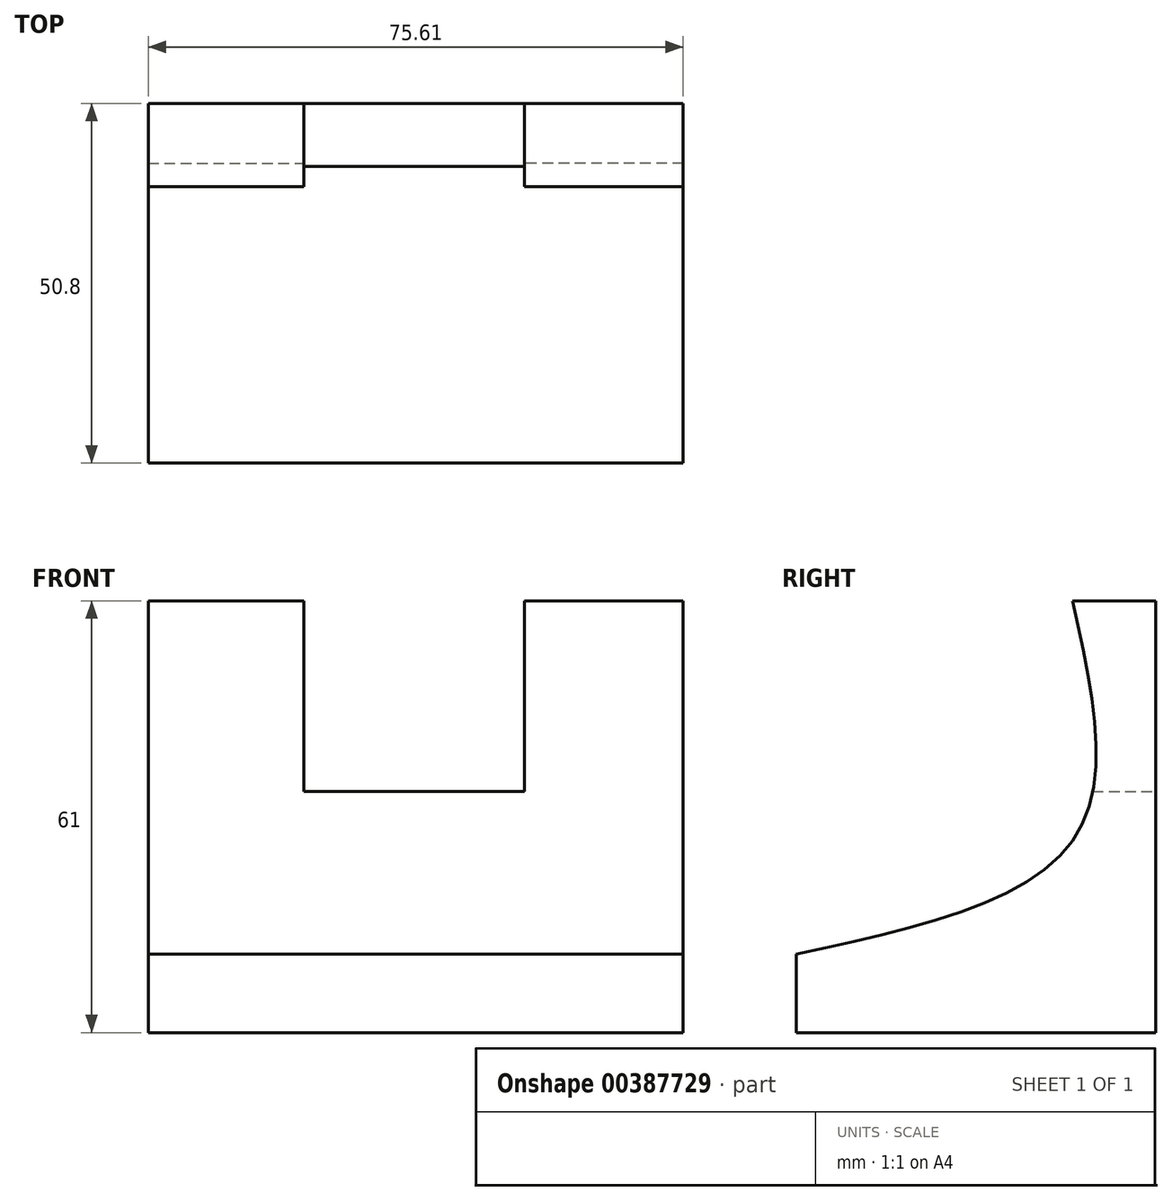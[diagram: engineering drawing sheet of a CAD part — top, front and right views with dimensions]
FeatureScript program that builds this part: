
annotation { "Feature Type Name" : "Feature", "Feature Type Description" : "" }
export const myFeature = defineFeature(function(context is Context, id is Id, definition is map)
    precondition{}
    {
        {
            var Q0;
            Q0=qCreatedBy(makeId("Front.planeOp"),FACE);
            var sketch = newSketch(context, id + "F0", { "sketchPlane" : qUnion([Q0])});
            skLineSegment(sketch, "E0", {"start": v(0, 0) * mm, "end": v(0, 61) * mm});
            skLineSegment(sketch, "E1", {"start": v(0, 61) * mm, "end": v(75.61, 61) * mm});
            skLineSegment(sketch, "E2", {"start": v(75.61, 61) * mm, "end": v(75.61, 0) * mm});
            skLineSegment(sketch, "E3", {"start": v(75.61, 0) * mm, "end": v(0, 0) * mm});
            skSolve(sketch);
        }
        {
            var Q0;
            Q0 = qSketchRegion(id + "F0", true);
            extrude(context, id + "F1", {"entities" : qUnion([Q0]), "depth" : 50.8 * mm});
        }
        {
            var Q0;
            Q0=makeQuery(id+"F1.opExtrude","SWEPT_FACE",FACE,{"disambiguationData":[OSD([sQuery(id+"F0.wireOp",EDGE,"E0")])]});
            var sketch = newSketch(context, id + "F2", { "sketchPlane" : qUnion([Q0])});
            skFitSpline(sketch, "E4", {"points": [v(11.77, 61) * mm, v(11.5, 27.52) * mm, v(50.8, 11.07) * mm], "startDerivative": vector(-18.17, -80.7) * mm, "endDerivative": vector(93.97, -20.38) * mm});
            skSolve(sketch);
        }
        {
            var Q0;
            {var subQ0=sQuery(id+"F2.wireOp",EDGE,"E4");Q0=makeQuery(id+"F2.imprint","IMPRINT",FACE,{"disambiguationData":[TD([[makeQuery(id+"F2.imprint","IMPRINT",EDGE,{"derivedFrom":subQ0}),1.0]])]});}
            extrude(context, id + "F3", {"entities" : qUnion([Q0]), "operationType" : NewBodyOperationType.REMOVE, "oppositeDirection" : true, "depth" : 76.2 * mm});
        }
        {
            var Q0;
            Q0=makeQuery(id+"F1.opExtrude","CAP_FACE",FACE,{"disambiguationData":[OSD([sQuery(id+"F0.wireOp",EDGE,"E0"),sQuery(id+"F0.wireOp",EDGE,"E1"),sQuery(id+"F0.wireOp",EDGE,"E2"),sQuery(id+"F0.wireOp",EDGE,"E3")])],"isStart":true});
            var sketch = newSketch(context, id + "F4", { "sketchPlane" : qUnion([Q0])});
            skLineSegment(sketch, "E5", {"start": v(-53.2, 61) * mm, "end": v(-53.2, 34.05) * mm});
            skLineSegment(sketch, "E6", {"start": v(-53.2, 34.05) * mm, "end": v(-21.99, 34.05) * mm});
            skLineSegment(sketch, "E7", {"start": v(-21.99, 34.05) * mm, "end": v(-21.99, 61) * mm});
            skSolve(sketch);
        }
        {
            var Q0;
            {var subQ0=sQuery(id+"F4.wireOp",EDGE,"E5");Q0=makeQuery(id+"F4.imprint","IMPRINT",FACE,{"disambiguationData":[TD([[makeQuery(id+"F4.imprint","IMPRINT",EDGE,{"derivedFrom":subQ0}),1.0]])]});}
            extrude(context, id + "F5", {"entities" : qUnion([Q0]), "operationType" : NewBodyOperationType.REMOVE, "oppositeDirection" : true, "depth" : 25.4 * mm});
        }
    });
